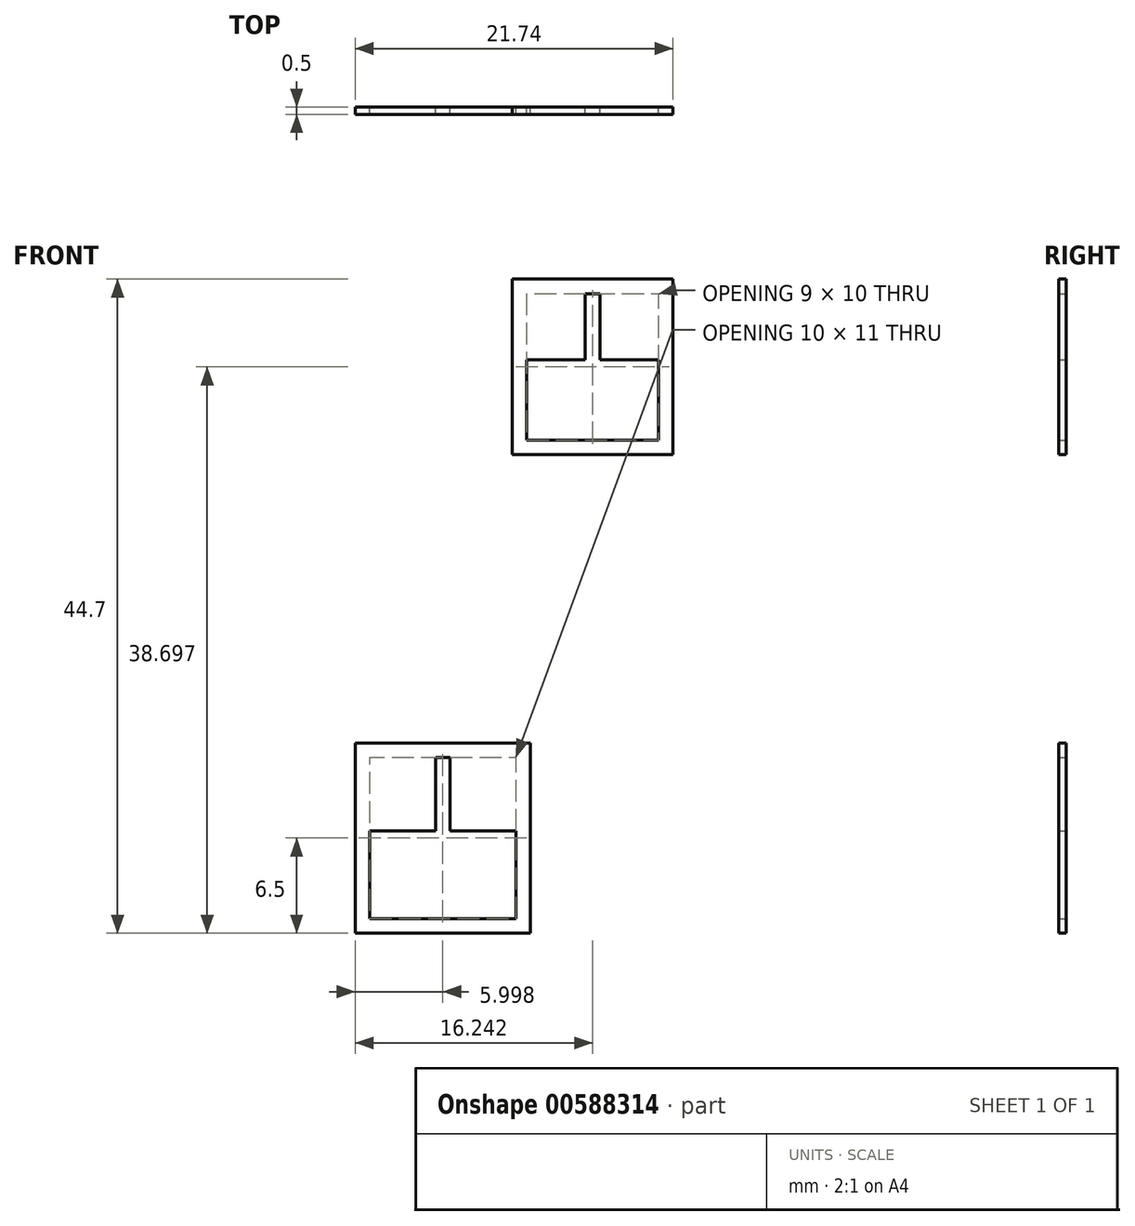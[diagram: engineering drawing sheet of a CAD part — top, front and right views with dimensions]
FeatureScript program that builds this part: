
annotation { "Feature Type Name" : "Feature", "Feature Type Description" : "" }
export const myFeature = defineFeature(function(context is Context, id is Id, definition is map)
    precondition{}
    {
        {
            var Q0;
            Q0=qCreatedBy(makeId("Front.planeOp"),FACE);
            var sketch = newSketch(context, id + "F0", { "sketchPlane" : qUnion([Q0])});
            skLineSegment(sketch, "E0.bottom", {"start": v(108.14, 31.7) * mm, "end": v(97.14, 31.7) * mm});
            skLineSegment(sketch, "E0.top", {"start": v(108.14, 19.7) * mm, "end": v(97.14, 19.7) * mm});
            skLineSegment(sketch, "E0.left", {"start": v(108.14, 31.7) * mm, "end": v(108.14, 19.7) * mm});
            skLineSegment(sketch, "E0.right", {"start": v(97.14, 31.7) * mm, "end": v(97.14, 19.7) * mm});
            skLineSegment(sketch, "E1.bottom", {"start": v(98.4, 0) * mm, "end": v(86.4, 0) * mm});
            skLineSegment(sketch, "E1.top", {"start": v(98.4, -13) * mm, "end": v(86.4, -13) * mm});
            skLineSegment(sketch, "E1.left", {"start": v(98.4, 0) * mm, "end": v(98.4, -13) * mm});
            skLineSegment(sketch, "E1.right", {"start": v(86.4, 0) * mm, "end": v(86.4, -13) * mm});
            skLineSegment(sketch, "E2.0", {"start": v(107.14, 30.7) * mm, "end": v(98.14, 30.7) * mm});
            skLineSegment(sketch, "E2.1", {"start": v(107.14, 30.7) * mm, "end": v(107.14, 20.7) * mm});
            skLineSegment(sketch, "E2.2", {"start": v(107.14, 20.7) * mm, "end": v(98.14, 20.7) * mm});
            skLineSegment(sketch, "E2.3", {"start": v(98.14, 30.7) * mm, "end": v(98.14, 20.7) * mm});
            skLineSegment(sketch, "E3.0", {"start": v(97.4, -1) * mm, "end": v(87.4, -1) * mm});
            skLineSegment(sketch, "E3.1", {"start": v(97.4, -1) * mm, "end": v(97.4, -12) * mm});
            skLineSegment(sketch, "E3.2", {"start": v(97.4, -12) * mm, "end": v(87.4, -12) * mm});
            skLineSegment(sketch, "E3.3", {"start": v(87.4, -1) * mm, "end": v(87.4, -12) * mm});
            skLineSegment(sketch, "E4.bottom", {"start": v(107.14, 30.7) * mm, "end": v(103.14, 30.7) * mm});
            skLineSegment(sketch, "E4.top", {"start": v(107.14, 26.2) * mm, "end": v(103.14, 26.2) * mm});
            skLineSegment(sketch, "E4.left", {"start": v(107.14, 30.7) * mm, "end": v(107.14, 26.2) * mm});
            skLineSegment(sketch, "E4.right", {"start": v(103.14, 30.7) * mm, "end": v(103.14, 26.2) * mm});
            skLineSegment(sketch, "E5.bottom", {"start": v(107.14, 20.7) * mm, "end": v(103.14, 20.7) * mm});
            skLineSegment(sketch, "E5.top", {"start": v(107.14, 25.2) * mm, "end": v(103.14, 25.2) * mm});
            skLineSegment(sketch, "E5.left", {"start": v(107.14, 20.7) * mm, "end": v(107.14, 25.2) * mm});
            skLineSegment(sketch, "E5.right", {"start": v(103.14, 20.7) * mm, "end": v(103.14, 25.2) * mm});
            skLineSegment(sketch, "E6.bottom", {"start": v(98.14, 30.7) * mm, "end": v(102.14, 30.7) * mm});
            skLineSegment(sketch, "E6.top", {"start": v(98.14, 26.2) * mm, "end": v(102.14, 26.2) * mm});
            skLineSegment(sketch, "E6.left", {"start": v(98.14, 30.7) * mm, "end": v(98.14, 26.2) * mm});
            skLineSegment(sketch, "E6.right", {"start": v(102.14, 30.7) * mm, "end": v(102.14, 26.2) * mm});
            skLineSegment(sketch, "E7.bottom", {"start": v(98.14, 20.7) * mm, "end": v(102.14, 20.7) * mm});
            skLineSegment(sketch, "E7.top", {"start": v(98.14, 25.2) * mm, "end": v(102.14, 25.2) * mm});
            skLineSegment(sketch, "E7.left", {"start": v(98.14, 20.7) * mm, "end": v(98.14, 25.2) * mm});
            skLineSegment(sketch, "E7.right", {"start": v(102.14, 20.7) * mm, "end": v(102.14, 25.2) * mm});
            skLineSegment(sketch, "E8.bottom", {"start": v(97.4, -1) * mm, "end": v(92.9, -1) * mm});
            skLineSegment(sketch, "E8.top", {"start": v(97.4, -6) * mm, "end": v(92.9, -6) * mm});
            skLineSegment(sketch, "E8.left", {"start": v(97.4, -1) * mm, "end": v(97.4, -6) * mm});
            skLineSegment(sketch, "E8.right", {"start": v(92.9, -1) * mm, "end": v(92.9, -6) * mm});
            skLineSegment(sketch, "E9.bottom", {"start": v(97.4, -12) * mm, "end": v(92.9, -12) * mm});
            skLineSegment(sketch, "E9.top", {"start": v(97.4, -7) * mm, "end": v(92.9, -7) * mm});
            skLineSegment(sketch, "E9.left", {"start": v(97.4, -12) * mm, "end": v(97.4, -7) * mm});
            skLineSegment(sketch, "E9.right", {"start": v(92.9, -12) * mm, "end": v(92.9, -7) * mm});
            skLineSegment(sketch, "E10.bottom", {"start": v(87.4, -1) * mm, "end": v(91.9, -1) * mm});
            skLineSegment(sketch, "E10.top", {"start": v(87.4, -6) * mm, "end": v(91.9, -6) * mm});
            skLineSegment(sketch, "E10.left", {"start": v(87.4, -1) * mm, "end": v(87.4, -6) * mm});
            skLineSegment(sketch, "E10.right", {"start": v(91.9, -1) * mm, "end": v(91.9, -6) * mm});
            skLineSegment(sketch, "E11.bottom", {"start": v(87.4, -12) * mm, "end": v(91.9, -12) * mm});
            skLineSegment(sketch, "E11.top", {"start": v(87.4, -7) * mm, "end": v(91.9, -7) * mm});
            skLineSegment(sketch, "E11.left", {"start": v(87.4, -12) * mm, "end": v(87.4, -7) * mm});
            skLineSegment(sketch, "E11.right", {"start": v(91.9, -12) * mm, "end": v(91.9, -7) * mm});
            skSolve(sketch);
        }
        {
            var Q0;
            Q0=makeQuery(id+"F0.imprint","IMPRINT",FACE,{"disambiguationData":[TD([[makeQuery(id+"F0.imprint","IMPRINT",EDGE,{"derivedFrom":sQuery(id+"F0.wireOp",EDGE,"E0.bottom")}),1.0]])]});
            var Q1;
            Q1=makeQuery(id+"F0.imprint","IMPRINT",FACE,{"disambiguationData":[TD([[makeQuery(id+"F0.imprint","IMPRINT",EDGE,{"derivedFrom":sQuery(id+"F0.wireOp",EDGE,"E2.0")}),1.0]])]});
            var Q2;
            Q2=makeQuery(id+"F0.imprint","IMPRINT",FACE,{"disambiguationData":[TD([[makeQuery(id+"F0.imprint","IMPRINT",EDGE,{"derivedFrom":sQuery(id+"F0.wireOp",EDGE,"E1.bottom")}),1.0]])]});
            var Q3;
            Q3=makeQuery(id+"F0.imprint","IMPRINT",FACE,{"disambiguationData":[TD([[makeQuery(id+"F0.imprint","IMPRINT",EDGE,{"derivedFrom":sQuery(id+"F0.wireOp",EDGE,"E3.0")}),1.0]])]});
            extrude(context, id + "F1", {"entities" : qUnion([Q0, Q1, Q2, Q3]), "depth" : .5 * mm, "offsetDistance" : 25 * mm});
        }
    });
